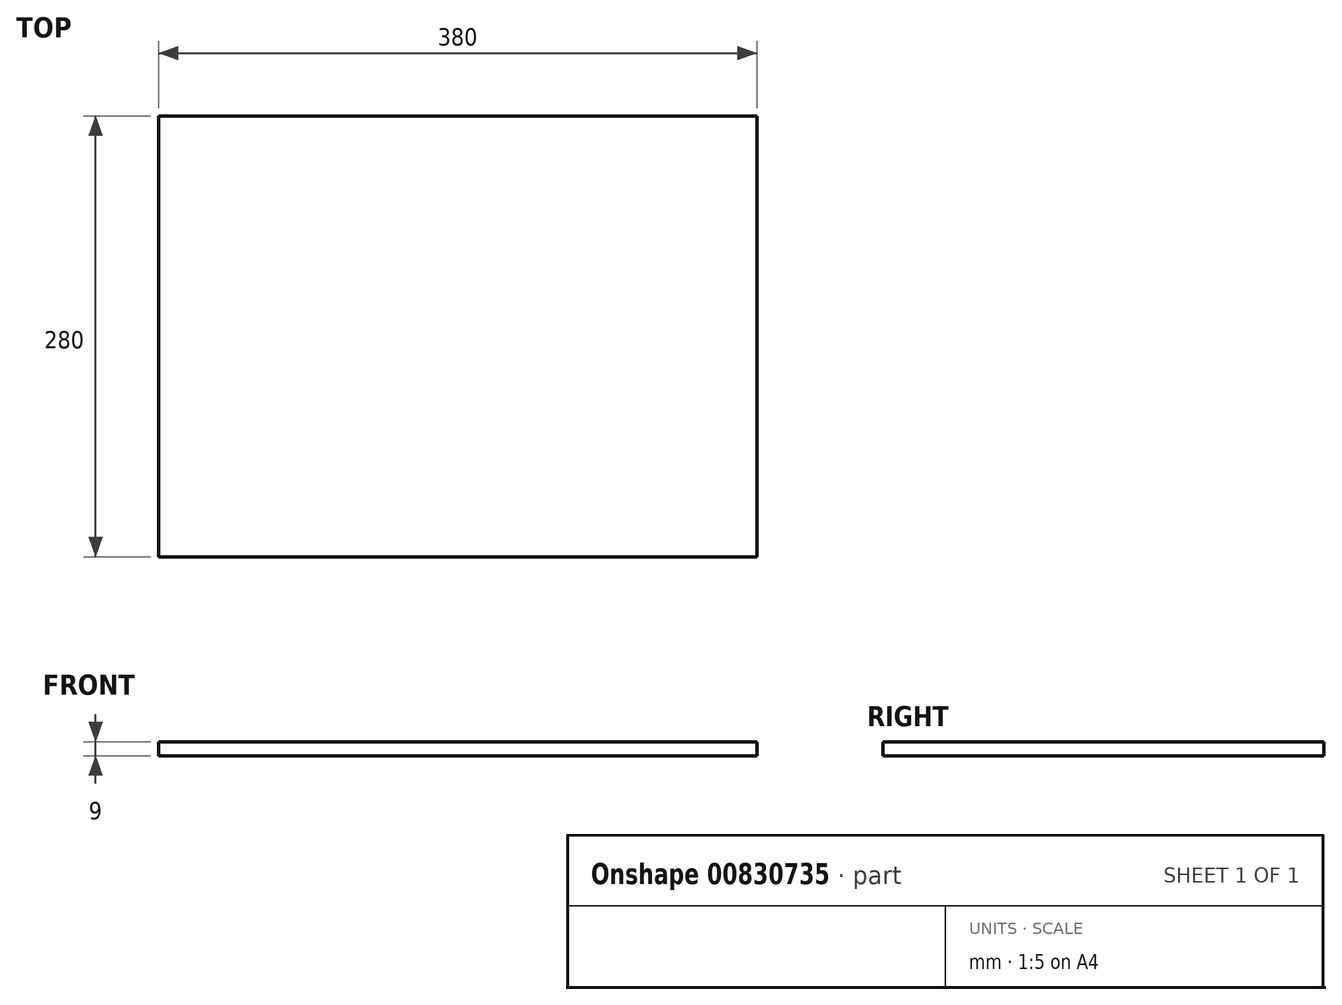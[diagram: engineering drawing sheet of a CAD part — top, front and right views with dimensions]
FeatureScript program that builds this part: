
annotation { "Feature Type Name" : "Feature", "Feature Type Description" : "" }
export const myFeature = defineFeature(function(context is Context, id is Id, definition is map)
    precondition{}
    {
        {
            var Q0;
            Q0=qCreatedBy(makeId("Top.planeOp"),FACE);
            var sketch = newSketch(context, id + "F0", { "sketchPlane" : qUnion([Q0])});
            skLineSegment(sketch, "E0.bottom", {"start": v(-220.28, 0) * mm, "end": v(159.72, 0) * mm});
            skLineSegment(sketch, "E0.top", {"start": v(-220.28, 280) * mm, "end": v(159.72, 280) * mm});
            skLineSegment(sketch, "E0.left", {"start": v(-220.28, 0) * mm, "end": v(-220.28, 280) * mm});
            skLineSegment(sketch, "E0.right", {"start": v(159.72, 0) * mm, "end": v(159.72, 280) * mm});
            skSolve(sketch);
        }
        {
            var Q0;
            Q0=makeQuery(id+"F0.imprint","IMPRINT",FACE,{"disambiguationData":[TD([[makeQuery(id+"F0.imprint","IMPRINT",EDGE,{"derivedFrom":sQuery(id+"F0.wireOp",EDGE,"E0.bottom")}),1.0]])]});
            extrude(context, id + "F1", {"entities" : qUnion([Q0]), "depth" : 9 * mm, "offsetDistance" : 25 * mm});
        }
    });
